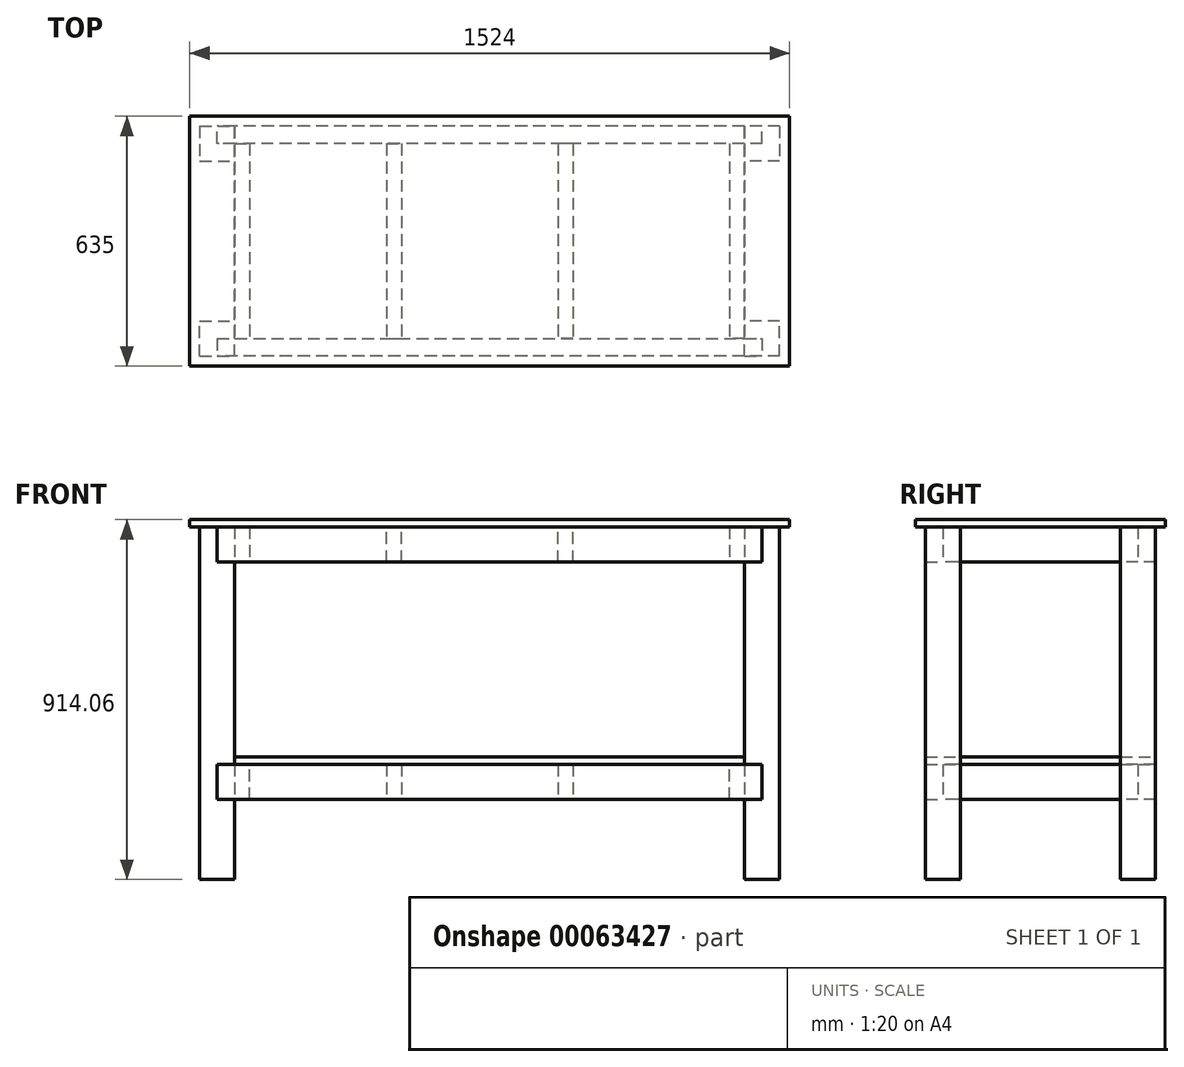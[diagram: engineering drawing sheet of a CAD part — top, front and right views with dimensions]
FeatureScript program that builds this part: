
annotation { "Feature Type Name" : "Feature", "Feature Type Description" : "" }
export const myFeature = defineFeature(function(context is Context, id is Id, definition is map)
    precondition{}
    {
        {
            var Q0;
            Q0=qCreatedBy(makeId("Top.planeOp"),FACE);
            var sketch = newSketch(context, id + "F0", { "sketchPlane" : qUnion([Q0])});
            skLineSegment(sketch, "E0.bottom", {"start": v(-762, -317.5) * mm, "end": v(762, -317.5) * mm});
            skLineSegment(sketch, "E0.top", {"start": v(-762, 317.5) * mm, "end": v(762, 317.5) * mm});
            skLineSegment(sketch, "E0.left", {"start": v(-762, -317.5) * mm, "end": v(-762, 317.5) * mm});
            skLineSegment(sketch, "E0.right", {"start": v(762, -317.5) * mm, "end": v(762, 317.5) * mm});
            skPoint(sketch, "E0.middle", {"position": v(0, 0) * mm});
            skSolve(sketch);
        }
        {
            var Q0;
            Q0 = qSketchRegion(id + "F0", true);
            extrude(context, id + "F1", {"entities" : qUnion([Q0]), "depth" : 19.05 * mm});
        }
        {
            var Q0;
            Q0=makeQuery(id+"F1.opExtrude","CAP_FACE",FACE,{"disambiguationData":[OSD([sQuery(id+"F0.wireOp",EDGE,"E0.bottom"),sQuery(id+"F0.wireOp",EDGE,"E0.top"),sQuery(id+"F0.wireOp",EDGE,"E0.left"),sQuery(id+"F0.wireOp",EDGE,"E0.right")])],"isStart":true});
            var sketch = newSketch(context, id + "F2", { "sketchPlane" : qUnion([Q0])});
            skLineSegment(sketch, "E1.bottom", {"start": v(-736.6, 292.1) * mm, "end": v(-647.7, 292.1) * mm});
            skLineSegment(sketch, "E1.top", {"start": v(-736.6, 203.2) * mm, "end": v(-647.7, 203.2) * mm});
            skLineSegment(sketch, "E1.left", {"start": v(-736.6, 292.1) * mm, "end": v(-736.6, 203.2) * mm});
            skLineSegment(sketch, "E1.right", {"start": v(-647.7, 292.1) * mm, "end": v(-647.7, 203.2) * mm});
            skLineSegment(sketch, "E2", {"start": v(0, 0) * mm, "end": v(0, 450.4) * mm, "construction": true});
            skLineSegment(sketch, "E3", {"start": v(0, 0) * mm, "end": v(-853.89, 0) * mm, "construction": true});
            skLineSegment(sketch, "E4.MirrorCS", {"start": v(736.6, 292.1) * mm, "end": v(647.7, 292.1) * mm});
            skLineSegment(sketch, "E5.MirrorCS", {"start": v(736.6, 203.2) * mm, "end": v(647.7, 203.2) * mm});
            skLineSegment(sketch, "E6.MirrorCS", {"start": v(736.6, 292.1) * mm, "end": v(736.6, 203.2) * mm});
            skLineSegment(sketch, "E7.MirrorCS", {"start": v(647.7, 292.1) * mm, "end": v(647.7, 203.2) * mm});
            skLineSegment(sketch, "E8.MirrorCS", {"start": v(-647.7, -292.1) * mm, "end": v(-647.7, -203.2) * mm});
            skLineSegment(sketch, "E9.MirrorCS", {"start": v(-736.6, -292.1) * mm, "end": v(-736.6, -203.2) * mm});
            skLineSegment(sketch, "E10.MirrorCS", {"start": v(-736.6, -203.2) * mm, "end": v(-647.7, -203.2) * mm});
            skLineSegment(sketch, "E11.MirrorCS", {"start": v(-736.6, -292.1) * mm, "end": v(-647.7, -292.1) * mm});
            skLineSegment(sketch, "E12.MirrorCS", {"start": v(736.6, -292.1) * mm, "end": v(647.7, -292.1) * mm});
            skLineSegment(sketch, "E13.MirrorCS", {"start": v(736.6, -203.2) * mm, "end": v(647.7, -203.2) * mm});
            skLineSegment(sketch, "E14.MirrorCS", {"start": v(736.6, -292.1) * mm, "end": v(736.6, -203.2) * mm});
            skLineSegment(sketch, "E15.MirrorCS", {"start": v(647.7, -292.1) * mm, "end": v(647.7, -203.2) * mm});
            skSolve(sketch);
        }
        {
            var Q0;
            Q0 = qSketchRegion(id + "F2", true);
            extrude(context, id + "F3", {"entities" : qUnion([Q0]), "depth" : 895 * mm});
        }
        {
            var Q0;
            Q0=makeQuery(id+"F3.opExtrude","SWEPT_FACE",FACE,{"disambiguationData":[OSD([sQuery(id+"F2.wireOp",EDGE,"E1.bottom")])]});
            var sketch = newSketch(context, id + "F4", { "sketchPlane" : qUnion([Q0])});
            skLineSegment(sketch, "E16.bottom", {"start": v(-692.15, 0) * mm, "end": v(692.15, 0) * mm});
            skLineSegment(sketch, "E16.top", {"start": v(-692.15, -88.9) * mm, "end": v(692.15, -88.9) * mm});
            skLineSegment(sketch, "E16.left", {"start": v(-692.15, 0) * mm, "end": v(-692.15, -88.9) * mm});
            skLineSegment(sketch, "E16.right", {"start": v(692.15, 0) * mm, "end": v(692.15, -88.9) * mm});
            skLineSegment(sketch, "E17.bottom", {"start": v(-692.15, -602.91) * mm, "end": v(692.15, -602.91) * mm});
            skLineSegment(sketch, "E17.top", {"start": v(-692.15, -691.81) * mm, "end": v(692.15, -691.81) * mm});
            skLineSegment(sketch, "E17.left", {"start": v(-692.15, -602.91) * mm, "end": v(-692.15, -691.81) * mm});
            skLineSegment(sketch, "E17.right", {"start": v(692.15, -602.91) * mm, "end": v(692.15, -691.81) * mm});
            skSolve(sketch);
        }
        {
            var Q0;
            Q0 = qSketchRegion(id + "F4", true);
            extrude(context, id + "F5", {"entities" : qUnion([Q0]), "operationType" : NewBodyOperationType.REMOVE, "oppositeDirection" : true, "depth" : 44.45 * mm});
        }
        {
            var Q0;
            Q0=makeQuery(id+"F3.opExtrude","SWEPT_FACE",FACE,{"disambiguationData":[OSD([sQuery(id+"F2.wireOp",EDGE,"E12.MirrorCS")])]});
            var sketch = newSketch(context, id + "F6", { "sketchPlane" : qUnion([Q0])});
            skLineSegment(sketch, "E18.bottom", {"start": v(-692.15, 0) * mm, "end": v(692.15, 0) * mm});
            skLineSegment(sketch, "E18.top", {"start": v(-692.15, -88.9) * mm, "end": v(692.15, -88.9) * mm});
            skLineSegment(sketch, "E18.left", {"start": v(-692.15, 0) * mm, "end": v(-692.15, -88.9) * mm});
            skLineSegment(sketch, "E18.right", {"start": v(692.15, 0) * mm, "end": v(692.15, -88.9) * mm});
            skLineSegment(sketch, "E19.bottom", {"start": v(-692.15, -602.91) * mm, "end": v(692.15, -602.91) * mm});
            skLineSegment(sketch, "E19.top", {"start": v(-692.15, -691.81) * mm, "end": v(692.15, -691.81) * mm});
            skLineSegment(sketch, "E19.left", {"start": v(-692.15, -602.91) * mm, "end": v(-692.15, -691.81) * mm});
            skLineSegment(sketch, "E19.right", {"start": v(692.15, -602.91) * mm, "end": v(692.15, -691.81) * mm});
            skSolve(sketch);
        }
        {
            var Q0;
            Q0 = qSketchRegion(id + "F6", true);
            extrude(context, id + "F7", {"entities" : qUnion([Q0]), "operationType" : NewBodyOperationType.REMOVE, "oppositeDirection" : true, "depth" : 44.45 * mm});
        }
        {
            var Q0;
            {var subQ0=sQuery(id+"F2.wireOp",EDGE,"E1.right");var subQ1=sQuery(id+"F4.wireOp",EDGE,"E16.top");var subQ2=sQuery(id+"F4.wireOp",EDGE,"E16.left");Q0=makeQuery(id+"F5.boolean.opBoolean","COPY",FACE,{"disambiguationData":[TD([makeQuery(id+"F3.opExtrude","SWEPT_FACE",FACE,{"disambiguationData":[OSD([subQ0])]})])],"derivedFrom":makeQuery(id+"F5.opExtrude","CAP_FACE",FACE,{"disambiguationData":[OSD([sQuery(id+"F4.wireOp",EDGE,"E16.bottom"),subQ1,subQ2,sQuery(id+"F4.wireOp",EDGE,"E16.right")])],"isStart":false})});}
            var sketch = newSketch(context, id + "F8", { "sketchPlane" : qUnion([Q0])});
            skLineSegment(sketch, "E20.bottom", {"start": v(-692.15, 0) * mm, "end": v(692.15, 0) * mm});
            skLineSegment(sketch, "E20.top", {"start": v(-692.15, -88.9) * mm, "end": v(692.15, -88.9) * mm});
            skLineSegment(sketch, "E20.left", {"start": v(-692.15, 0) * mm, "end": v(-692.15, -88.9) * mm});
            skLineSegment(sketch, "E20.right", {"start": v(692.15, 0) * mm, "end": v(692.15, -88.9) * mm});
            skLineSegment(sketch, "E21.bottom", {"start": v(-692.15, -602.91) * mm, "end": v(692.15, -602.91) * mm});
            skLineSegment(sketch, "E21.top", {"start": v(-692.15, -691.81) * mm, "end": v(692.15, -691.81) * mm});
            skLineSegment(sketch, "E21.left", {"start": v(-692.15, -602.91) * mm, "end": v(-692.15, -691.81) * mm});
            skLineSegment(sketch, "E21.right", {"start": v(692.15, -602.91) * mm, "end": v(692.15, -691.81) * mm});
            skSolve(sketch);
        }
        {
            var Q0;
            Q0 = qSketchRegion(id + "F8", true);
            var Q1;
            Q1=makeQuery(id+"F3.opExtrude","SWEPT_FACE",FACE,{"disambiguationData":[OSD([sQuery(id+"F2.wireOp",EDGE,"E4.MirrorCS")])]});
            extrude(context, id + "F9", {"entities" : qUnion([Q0]), "endBound" : BoundingType.UP_TO_SURFACE, "endBoundEntityFace" : qUnion([Q1]), "depth" : 25.4 * mm});
        }
        {
            var Q0;
            {var subQ0=sQuery(id+"F2.wireOp",EDGE,"E15.MirrorCS");var subQ1=sQuery(id+"F6.wireOp",EDGE,"E18.top");var subQ2=sQuery(id+"F6.wireOp",EDGE,"E18.left");Q0=makeQuery(id+"F7.boolean.opBoolean","COPY",FACE,{"disambiguationData":[TD([makeQuery(id+"F3.opExtrude","SWEPT_FACE",FACE,{"disambiguationData":[OSD([subQ0])]})])],"derivedFrom":makeQuery(id+"F7.opExtrude","CAP_FACE",FACE,{"disambiguationData":[OSD([sQuery(id+"F6.wireOp",EDGE,"E18.bottom"),subQ1,subQ2,sQuery(id+"F6.wireOp",EDGE,"E18.right")])],"isStart":false})});}
            var sketch = newSketch(context, id + "F10", { "sketchPlane" : qUnion([Q0])});
            skLineSegment(sketch, "E22.bottom", {"start": v(-692.15, 0) * mm, "end": v(692.15, 0) * mm});
            skLineSegment(sketch, "E22.top", {"start": v(-692.15, -88.9) * mm, "end": v(692.15, -88.9) * mm});
            skLineSegment(sketch, "E22.left", {"start": v(-692.15, 0) * mm, "end": v(-692.15, -88.9) * mm});
            skLineSegment(sketch, "E22.right", {"start": v(692.15, 0) * mm, "end": v(692.15, -88.9) * mm});
            skLineSegment(sketch, "E23.bottom", {"start": v(-692.15, -602.91) * mm, "end": v(692.15, -602.91) * mm});
            skLineSegment(sketch, "E23.top", {"start": v(-692.15, -691.81) * mm, "end": v(692.15, -691.81) * mm});
            skLineSegment(sketch, "E23.left", {"start": v(-692.15, -602.91) * mm, "end": v(-692.15, -691.81) * mm});
            skLineSegment(sketch, "E23.right", {"start": v(692.15, -602.91) * mm, "end": v(692.15, -691.81) * mm});
            skSolve(sketch);
        }
        {
            var Q0;
            Q0 = qSketchRegion(id + "F10", true);
            var Q1;
            Q1=makeQuery(id+"F3.opExtrude","SWEPT_FACE",FACE,{"disambiguationData":[OSD([sQuery(id+"F2.wireOp",EDGE,"E12.MirrorCS")])]});
            extrude(context, id + "F11", {"entities" : qUnion([Q0]), "endBound" : BoundingType.UP_TO_SURFACE, "endBoundEntityFace" : qUnion([Q1]), "depth" : 25.4 * mm});
        }
        {
            var Q0;
            Q0=makeQuery(id+"F9.opExtrude","CAP_FACE",FACE,{"disambiguationData":[OSD([sQuery(id+"F8.wireOp",EDGE,"E20.bottom"),sQuery(id+"F8.wireOp",EDGE,"E20.top"),sQuery(id+"F8.wireOp",EDGE,"E20.left"),sQuery(id+"F8.wireOp",EDGE,"E20.right")])],"isStart":true});
            var sketch = newSketch(context, id + "F12", { "sketchPlane" : qUnion([Q0])});
            skLineSegment(sketch, "E24.bottom", {"start": v(-647.7, 0) * mm, "end": v(-609.6, 0) * mm});
            skLineSegment(sketch, "E24.top", {"start": v(-647.7, -88.9) * mm, "end": v(-609.6, -88.9) * mm});
            skLineSegment(sketch, "E24.left", {"start": v(-647.7, 0) * mm, "end": v(-647.7, -88.9) * mm});
            skLineSegment(sketch, "E24.right", {"start": v(-609.6, 0) * mm, "end": v(-609.6, -88.9) * mm});
            skLineSegment(sketch, "E25.bottom", {"start": v(647.7, 0) * mm, "end": v(609.6, 0) * mm});
            skLineSegment(sketch, "E25.top", {"start": v(647.7, -88.9) * mm, "end": v(609.6, -88.9) * mm});
            skLineSegment(sketch, "E25.left", {"start": v(647.7, 0) * mm, "end": v(647.7, -88.9) * mm});
            skLineSegment(sketch, "E25.right", {"start": v(609.6, 0) * mm, "end": v(609.6, -88.9) * mm});
            skLineSegment(sketch, "E26.bottom", {"start": v(-211.66, -88.9) * mm, "end": v(-173.56, -88.9) * mm});
            skLineSegment(sketch, "E26.top", {"start": v(-211.66, 0) * mm, "end": v(-173.56, 0) * mm});
            skLineSegment(sketch, "E26.left", {"start": v(-211.66, -88.9) * mm, "end": v(-211.66, 0) * mm});
            skLineSegment(sketch, "E26.right", {"start": v(-173.56, -88.9) * mm, "end": v(-173.56, 0) * mm});
            skLineSegment(sketch, "E27.bottom", {"start": v(224.38, -88.9) * mm, "end": v(262.48, -88.9) * mm});
            skLineSegment(sketch, "E27.top", {"start": v(224.38, 0) * mm, "end": v(262.48, 0) * mm});
            skLineSegment(sketch, "E27.left", {"start": v(224.38, -88.9) * mm, "end": v(224.38, 0) * mm});
            skLineSegment(sketch, "E27.right", {"start": v(262.48, -88.9) * mm, "end": v(262.48, 0) * mm});
            skLineSegment(sketch, "E28", {"start": v(-647.7, -88.9) * mm, "end": v(-647.7, -602.91) * mm, "construction": true});
            skLineSegment(sketch, "E29", {"start": v(-647.7, -345.9) * mm, "end": v(647.7, -345.9) * mm, "construction": true});
            skLineSegment(sketch, "E30.MirrorCS", {"start": v(224.38, -602.91) * mm, "end": v(262.48, -602.91) * mm});
            skLineSegment(sketch, "E31.MirrorCS", {"start": v(-211.66, -691.81) * mm, "end": v(-173.56, -691.81) * mm});
            skLineSegment(sketch, "E32.MirrorCS", {"start": v(-647.7, -602.91) * mm, "end": v(-609.6, -602.91) * mm});
            skLineSegment(sketch, "E33.MirrorCS", {"start": v(224.38, -691.81) * mm, "end": v(262.48, -691.81) * mm});
            skLineSegment(sketch, "E34.MirrorCS", {"start": v(-211.66, -602.91) * mm, "end": v(-173.56, -602.91) * mm});
            skLineSegment(sketch, "E35.MirrorCS", {"start": v(-647.7, -691.81) * mm, "end": v(-609.6, -691.81) * mm});
            skLineSegment(sketch, "E36.MirrorCS", {"start": v(647.7, -602.91) * mm, "end": v(609.6, -602.91) * mm});
            skLineSegment(sketch, "E37.MirrorCS", {"start": v(647.7, -691.81) * mm, "end": v(609.6, -691.81) * mm});
            skLineSegment(sketch, "E38.MirrorCS", {"start": v(-173.56, -602.91) * mm, "end": v(-173.56, -691.81) * mm});
            skLineSegment(sketch, "E39.MirrorCS", {"start": v(609.6, -691.81) * mm, "end": v(609.6, -602.91) * mm});
            skLineSegment(sketch, "E40.MirrorCS", {"start": v(-647.7, -602.91) * mm, "end": v(-647.7, -88.9) * mm, "construction": true});
            skLineSegment(sketch, "E41.MirrorCS", {"start": v(-211.66, -602.91) * mm, "end": v(-211.66, -691.81) * mm});
            skLineSegment(sketch, "E42.MirrorCS", {"start": v(224.38, -602.91) * mm, "end": v(224.38, -691.81) * mm});
            skLineSegment(sketch, "E43.MirrorCS", {"start": v(262.48, -602.91) * mm, "end": v(262.48, -691.81) * mm});
            skLineSegment(sketch, "E44.MirrorCS", {"start": v(647.7, -691.81) * mm, "end": v(647.7, -602.91) * mm});
            skLineSegment(sketch, "E45.MirrorCS", {"start": v(-609.6, -691.81) * mm, "end": v(-609.6, -602.91) * mm});
            skLineSegment(sketch, "E46.MirrorCS", {"start": v(-647.7, -691.81) * mm, "end": v(-647.7, -602.91) * mm});
            skSolve(sketch);
        }
        {
            var Q0;
            Q0 = qSketchRegion(id + "F12", true);
            var Q1;
            Q1=makeQuery(id+"F11.opExtrude","CAP_FACE",FACE,{"disambiguationData":[OSD([sQuery(id+"F10.wireOp",EDGE,"E22.bottom"),sQuery(id+"F10.wireOp",EDGE,"E22.top"),sQuery(id+"F10.wireOp",EDGE,"E22.left"),sQuery(id+"F10.wireOp",EDGE,"E22.right")])],"isStart":true});
            extrude(context, id + "F13", {"entities" : qUnion([Q0]), "endBound" : BoundingType.UP_TO_SURFACE, "endBoundEntityFace" : qUnion([Q1]), "depth" : 25.4 * mm});
        }
        {
            var Q0;
            Q0=makeQuery(id+"F9.opExtrude","SWEPT_FACE",FACE,{"disambiguationData":[OSD([sQuery(id+"F8.wireOp",EDGE,"E21.bottom")])]});
            var sketch = newSketch(context, id + "F14", { "sketchPlane" : qUnion([Q0])});
            skLineSegment(sketch, "E47.bottom", {"start": v(647.7, -292.1) * mm, "end": v(-647.7, -292.1) * mm});
            skLineSegment(sketch, "E47.top", {"start": v(647.7, 292.1) * mm, "end": v(-647.7, 292.1) * mm});
            skLineSegment(sketch, "E47.left", {"start": v(647.7, -292.1) * mm, "end": v(647.7, 292.1) * mm});
            skLineSegment(sketch, "E47.right", {"start": v(-647.7, -292.1) * mm, "end": v(-647.7, 292.1) * mm});
            skSolve(sketch);
        }
        {
            var Q0;
            Q0 = qSketchRegion(id + "F14", true);
            extrude(context, id + "F15", {"entities" : qUnion([Q0]), "depth" : 19.05 * mm});
        }
    });
